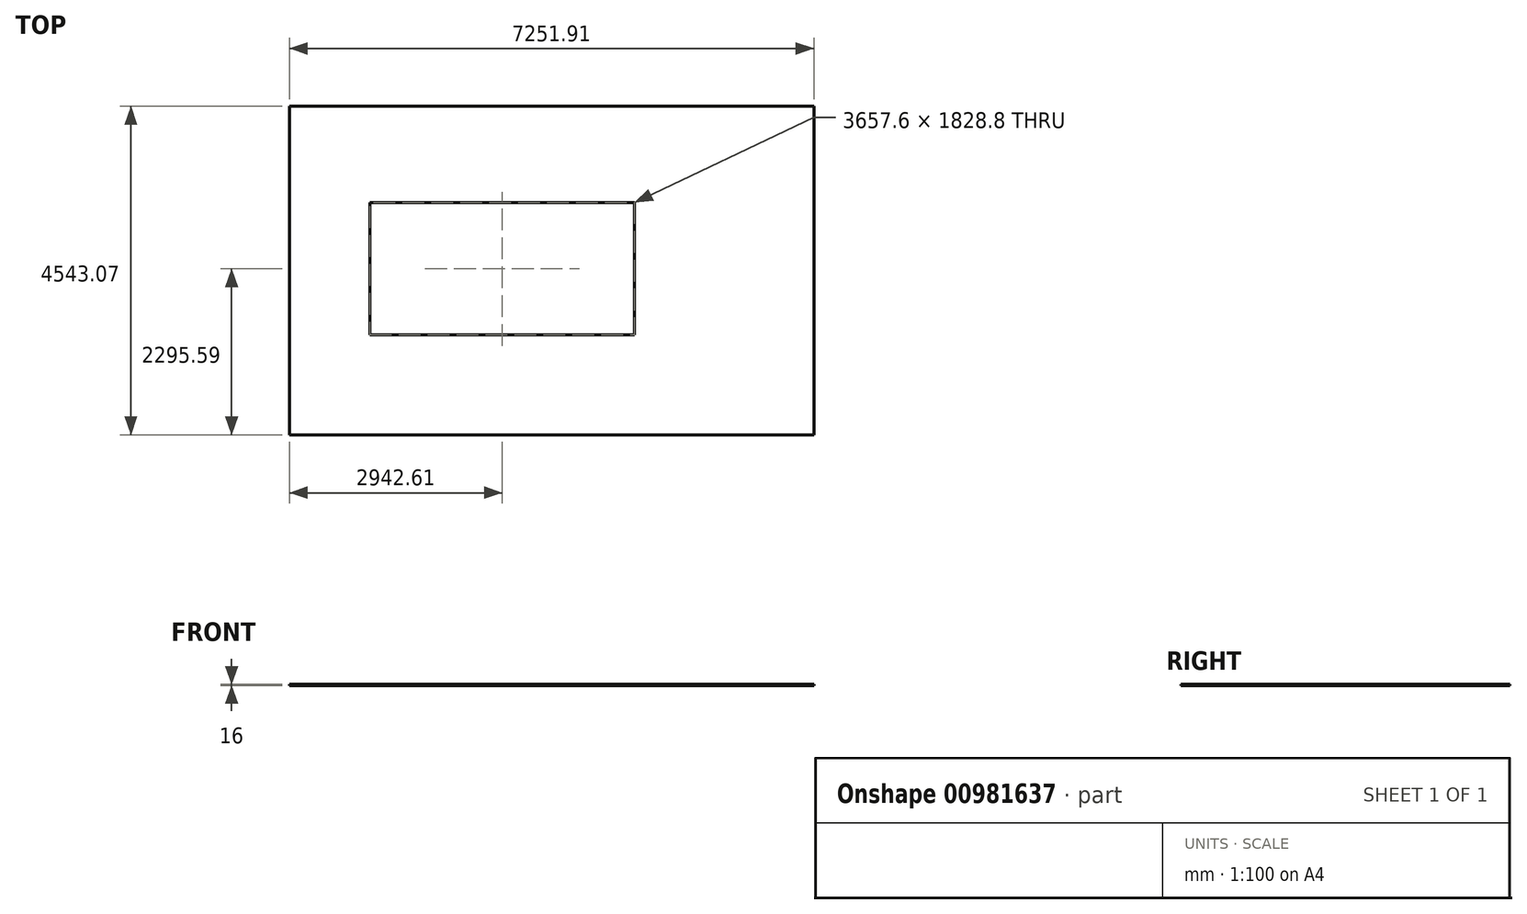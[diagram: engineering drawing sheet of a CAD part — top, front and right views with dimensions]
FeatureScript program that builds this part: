
annotation { "Feature Type Name" : "Feature", "Feature Type Description" : "" }
export const myFeature = defineFeature(function(context is Context, id is Id, definition is map)
    precondition{}
    {
        {
            var Q0;
            Q0=qCreatedBy(makeId("Top.planeOp"),FACE);
            var sketch = newSketch(context, id + "F0", { "sketchPlane" : qUnion([Q0])});
            skLineSegment(sketch, "E0", {"start": v(-2865.48, -33.76) * mm, "end": v(-2865.48, -1862.56) * mm});
            skLineSegment(sketch, "E1", {"start": v(-2865.48, -1862.56) * mm, "end": v(792.12, -1862.56) * mm});
            skLineSegment(sketch, "E2", {"start": v(792.12, -1862.56) * mm, "end": v(792.12, -33.76) * mm});
            skLineSegment(sketch, "E3", {"start": v(792.12, -33.76) * mm, "end": v(-1366.88, -33.76) * mm});
            skLineSegment(sketch, "E4", {"start": v(-1366.88, -33.76) * mm, "end": v(-1366.88, -33.76) * mm});
            skLineSegment(sketch, "E5", {"start": v(-1366.88, -33.76) * mm, "end": v(-2865.48, -33.76) * mm});
            skLineSegment(sketch, "E6.bottom", {"start": v(-3979.29, 1299.33) * mm, "end": v(3272.62, 1299.33) * mm});
            skLineSegment(sketch, "E6.top", {"start": v(-3979.29, -3243.74) * mm, "end": v(3272.62, -3243.74) * mm});
            skLineSegment(sketch, "E6.left", {"start": v(-3979.29, 1299.33) * mm, "end": v(-3979.29, -3243.74) * mm});
            skLineSegment(sketch, "E6.right", {"start": v(3272.62, 1299.33) * mm, "end": v(3272.62, -3243.74) * mm});
            skSolve(sketch);
        }
        {
            var Q0;
            Q0=makeQuery(id+"F0.imprint","IMPRINT",FACE,{"disambiguationData":[TD([[makeQuery(id+"F0.imprint","IMPRINT",EDGE,{"derivedFrom":sQuery(id+"F0.wireOp",EDGE,"E0")}),-1.0]])]});
            extrude(context, id + "F1", {"entities" : qUnion([Q0]), "depth" : 16 * mm, "offsetDistance" : 25 * mm});
        }
    });
